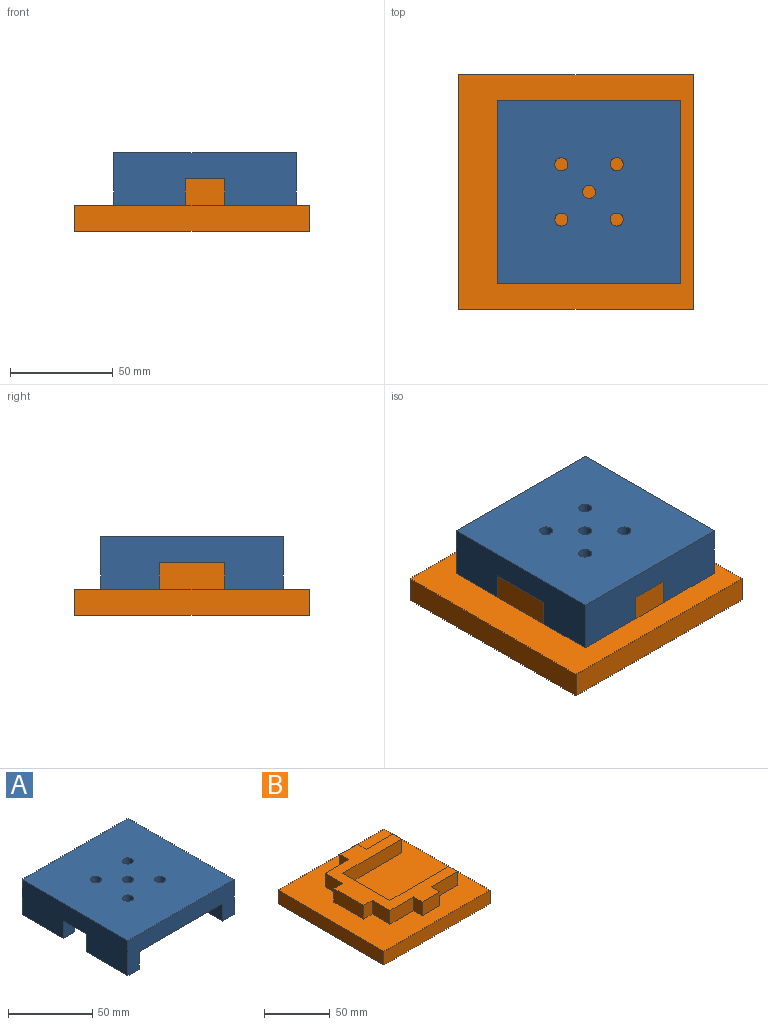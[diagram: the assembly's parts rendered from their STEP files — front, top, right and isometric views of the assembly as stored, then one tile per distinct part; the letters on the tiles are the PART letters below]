
ASSEMBLY  parts=2 mates=1
PART A: 27 faces, bbox 88.9x88.9x25.4 mm
  f0: plane 88.9x25.4mm, normal (0,1,0), area 1854.8mm2, adj f1,f8,f9,f10,f17,f21,f23,f26
  f1: plane 88.9x25.4mm, normal (-1,0,0), area 2016.1mm2, adj f0,f2,f9,f10,f11,f13,f20,f21
  f2: plane 88.9x25.4mm, normal (0,-1,0), area 1371mm2, adj f1,f8,f9,f10,f12,f13,f14,f16
  f3: cylinder r=3.17mm len=12.7mm, axis (0,0,-1), area 253.4mm2, adj f9,f10
  f4: cylinder r=3.17mm len=12.7mm, axis (0,0,-1), area 253.4mm2, adj f9,f10
  f5: cylinder r=3.17mm len=12.7mm, axis (0,0,-1), area 253.4mm2, adj f9,f10
  f6: cylinder r=3.17mm len=12.7mm, axis (0,0,-1), area 253.4mm2, adj f9,f10
  f7: cylinder r=3.17mm len=12.7mm, axis (0,0,-1), area 253.4mm2, adj f9,f10
  f8: plane 88.9x25.4mm, normal (1,0,0), area 2016.1mm2, adj f0,f2,f9,f10,f15,f16,f24,f26
  f9: plane 88.9x88.9mm, normal (0,0,1), area 7744.9mm2, adj f0,f1,f2,f3,f4,f5,f6,f7
  f10: plane 88.9x88.9mm, normal (0,0,-1), area 6051.3mm2, adj f0,f1,f2,f3,f4,f5,f6,f7
  f11: plane 12.7x9.53mm, normal (0,1,0), area 121mm2, adj f1,f10,f12,f13
  f12: plane 34.93x12.7mm, normal (1,0,0), area 443.5mm2, adj f2,f10,f11,f13
  f13: plane 34.93x9.53mm, normal (0,0,-1), area 332.7mm2, adj f1,f2,f11,f12
  f14: plane 34.93x12.7mm, normal (-1,0,0), area 443.5mm2, adj f2,f10,f15,f16
  f15: plane 12.7x9.53mm, normal (0,1,0), area 121mm2, adj f8,f10,f14,f16
  f16: plane 34.93x9.53mm, normal (0,0,-1), area 332.7mm2, adj f2,f8,f14,f15
  f17: plane 12.7x9.53mm, normal (1,0,0), area 121mm2, adj f0,f10,f18,f21
  f18: plane 19.05x12.7mm, normal (0,-1,0), area 241.9mm2, adj f10,f17,f19,f21
  f19: plane 25.4x12.7mm, normal (1,0,0), area 322.6mm2, adj f10,f18,f20,f21
  f20: plane 12.7x9.53mm, normal (0,-1,0), area 121mm2, adj f1,f10,f19,f21
  f21: plane 34.93x28.58mm, normal (0,0,-1), area 514.1mm2, adj f0,f1,f17,f18,f19,f20
  f22: plane 19.05x12.7mm, normal (0,-1,0), area 241.9mm2, adj f10,f23,f25,f26
  f23: plane 12.7x9.53mm, normal (-1,0,0), area 121mm2, adj f0,f10,f22,f26
  f24: plane 12.7x9.53mm, normal (0,-1,0), area 121mm2, adj f8,f10,f25,f26
  f25: plane 25.4x12.7mm, normal (-1,0,0), area 322.6mm2, adj f10,f22,f24,f26
  f26: plane 34.93x28.58mm, normal (0,0,-1), area 514.1mm2, adj f0,f8,f22,f23,f24,f25
PART B: 27 faces, bbox 114.3x114.3x25.4 mm
  f0: plane 114.3x114.3mm, normal (0,0,1), area 10524.2mm2, adj f1,f2,f3,f4,f6,f7,f8,f9
  f1: plane 114.3x12.7mm, normal (0,-1,0), area 1451.6mm2, adj f0,f2,f4,f5
  f2: plane 114.3x12.7mm, normal (1,0,0), area 1451.6mm2, adj f0,f1,f3,f5
  f3: plane 114.3x12.7mm, normal (0,1,0), area 1451.6mm2, adj f0,f2,f4,f5
  f4: plane 114.3x12.7mm, normal (-1,0,0), area 1451.6mm2, adj f0,f1,f3,f5
  f5: plane 114.3x114.3mm, normal (0,0,-1), area 13064.5mm2, adj f1,f2,f3,f4
  f6: plane 12.7x9.53mm, normal (0,-1,0), area 121mm2, adj f0,f7,f25,f26
  f7: plane 19.05x12.7mm, normal (-1,0,0), area 241.9mm2, adj f0,f6,f8,f26
  f8: plane 25.4x12.7mm, normal (0,-1,0), area 322.6mm2, adj f0,f7,f9,f26
  f9: plane 12.7x9.53mm, normal (-1,0,0), area 121mm2, adj f0,f8,f10,f26
  f10: plane 19.05x12.7mm, normal (0,-1,0), area 241.9mm2, adj f0,f9,f11,f26
  f11: plane 12.7x9.53mm, normal (1,0,0), area 121mm2, adj f0,f10,f12,f26
  f12: plane 28.58x12.7mm, normal (0,-1,0), area 362.9mm2, adj f0,f11,f13,f26
  f13: plane 12.7x9.53mm, normal (1,0,0), area 121mm2, adj f0,f12,f14,f26
  f14: plane 63.5x12.7mm, normal (0,1,0), area 806.5mm2, adj f0,f13,f15,f26
  f15: plane 50.8x12.7mm, normal (1,0,0), area 645.2mm2, adj f0,f14,f16,f26
  f16: plane 63.5x12.7mm, normal (0,-1,0), area 806.5mm2, adj f0,f15,f17,f26
  f17: plane 12.7x9.53mm, normal (1,0,0), area 121mm2, adj f0,f16,f18,f26
  f18: plane 28.58x12.7mm, normal (0,1,0), area 362.9mm2, adj f0,f17,f19,f26
  f19: plane 12.7x9.53mm, normal (1,0,0), area 121mm2, adj f0,f18,f20,f26
  f20: plane 19.05x12.7mm, normal (0,1,0), area 241.9mm2, adj f0,f19,f21,f26
  f21: plane 12.7x9.53mm, normal (-1,0,0), area 121mm2, adj f0,f20,f22,f26
  f22: plane 25.4x12.7mm, normal (0,1,0), area 322.6mm2, adj f0,f21,f23,f26
  f23: plane 19.05x12.7mm, normal (-1,0,0), area 241.9mm2, adj f0,f22,f24,f26
  f24: plane 12.7x9.53mm, normal (0,1,0), area 121mm2, adj f0,f23,f25,f26
  f25: plane 31.75x12.7mm, normal (-1,0,0), area 403.2mm2, adj f0,f6,f24,f26
  f26: plane 88.9x82.55mm, normal (0,0,1), area 2540.3mm2, adj f6,f7,f8,f9,f10,f11,f12,f13
PLACE A rot(axis=(0,0,1),90deg) t=(6.35,0,25.4)mm
PLACE B at identity
MATE fastened B.f26 <-> A.f10  axis (0,0,1) through (-38.1,0,25.4)mm
